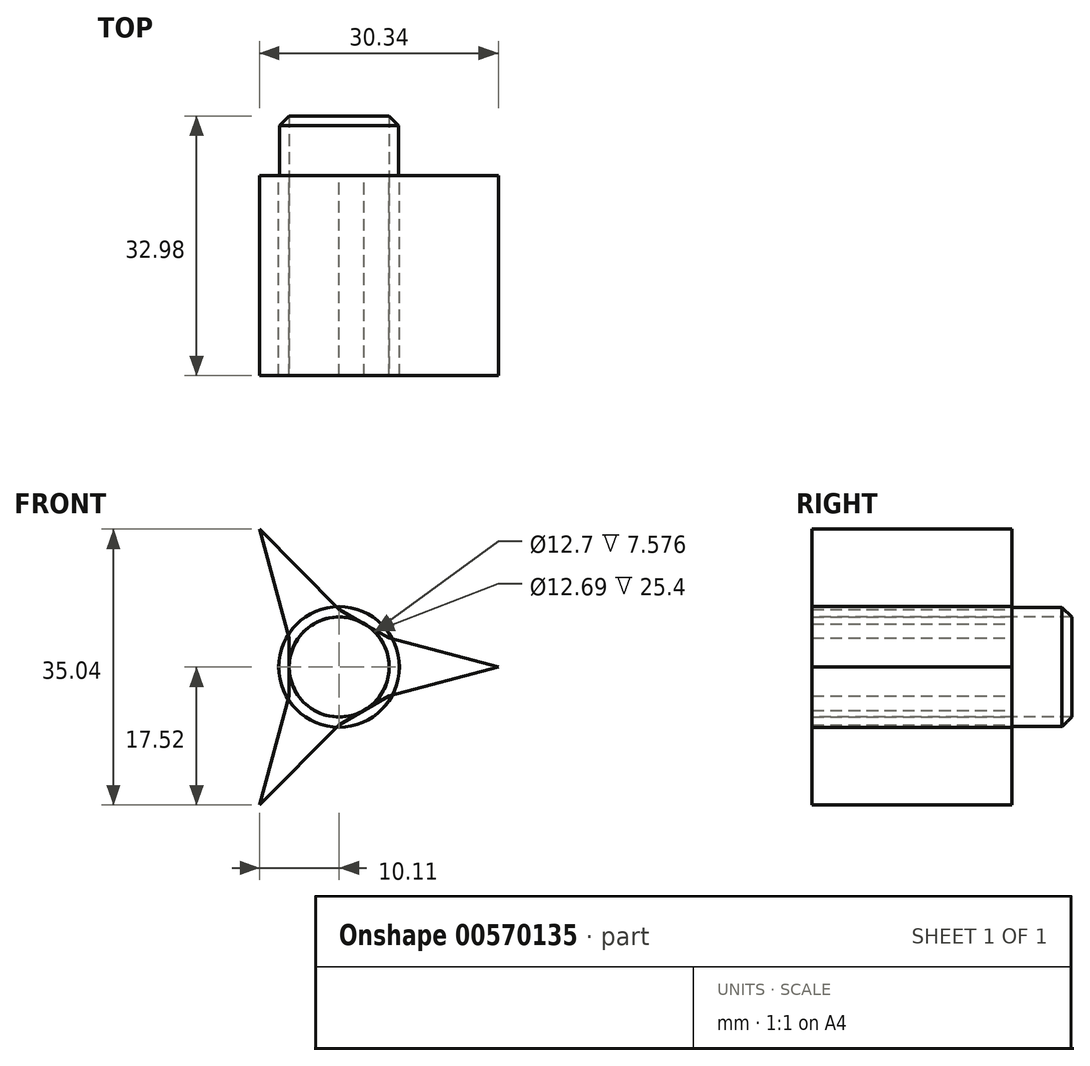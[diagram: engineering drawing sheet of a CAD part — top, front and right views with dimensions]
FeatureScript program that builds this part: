
annotation { "Feature Type Name" : "Feature", "Feature Type Description" : "" }
export const myFeature = defineFeature(function(context is Context, id is Id, definition is map)
    precondition{}
    {
        {
            var Q0;
            Q0=qCreatedBy(makeId("Front.planeOp"),FACE);
            var sketch = newSketch(context, id + "F0", { "sketchPlane" : qUnion([Q0])});
            skCircle(sketch, "E0", {"center": v(0, 0) * mm, "radius": 6.35 * mm});
            skPoint(sketch, "E1.0.midPoint", {"position": v(15.37, 8.44) * mm});
            skArc(sketch, "E2.cCircle", {"start": v(-8.14, 15.53) * mm, "mid": v(-8.77, 15.18) * mm, "end": v(-9.38, 14.81) * mm, "construction": true});
            skCircle(sketch, "E3.cCircle", {"center": v(0, 0) * mm, "radius": 6.35 * mm, "construction": true});
            skLineSegment(sketch, "E3.0", {"start": v(6.35, 3.67) * mm, "end": v(6.35, -3.67) * mm});
            skLineSegment(sketch, "E3.1", {"start": v(6.35, -3.67) * mm, "end": v(0, -7.33) * mm});
            skLineSegment(sketch, "E3.2", {"start": v(0, -7.33) * mm, "end": v(-6.35, -3.67) * mm});
            skLineSegment(sketch, "E3.3", {"start": v(-6.35, -3.67) * mm, "end": v(-6.35, 3.67) * mm});
            skLineSegment(sketch, "E3.4", {"start": v(-6.35, 3.67) * mm, "end": v(0, 7.33) * mm});
            skLineSegment(sketch, "E3.5", {"start": v(0, 7.33) * mm, "end": v(6.35, 3.67) * mm});
            skPoint(sketch, "E3.0.midPoint", {"position": v(6.35, 0) * mm});
            skLineSegment(sketch, "E4", {"start": v(-10.11, 17.52) * mm, "end": v(-6.35, 3.67) * mm});
            skLineSegment(sketch, "E5", {"start": v(-10.11, 17.52) * mm, "end": v(0, 7.33) * mm});
            skLineSegment(sketch, "E6", {"start": v(6.35, 3.67) * mm, "end": v(20.23, 0) * mm});
            skLineSegment(sketch, "E7", {"start": v(6.35, -3.67) * mm, "end": v(20.23, 0) * mm});
            skLineSegment(sketch, "E8", {"start": v(0, -7.33) * mm, "end": v(-10.11, -17.52) * mm});
            skLineSegment(sketch, "E9", {"start": v(-6.35, -3.67) * mm, "end": v(-10.11, -17.52) * mm});
            skPoint(sketch, "E10.orphan", {"position": v(10.5, 16.88) * mm});
            skArc(sketch, "E11.trimOffspring", {"start": v(17.52, -0.72) * mm, "mid": v(17.53, 0) * mm, "end": v(17.52, 0.72) * mm, "construction": true});
            skArc(sketch, "E12.trimOffspring", {"start": v(-9.38, -14.81) * mm, "mid": v(-8.77, -15.18) * mm, "end": v(-8.14, -15.53) * mm, "construction": true});
            skPoint(sketch, "E13.orphan", {"position": v(-20.16, -0.24) * mm});
            skSolve(sketch);
        }
        {
            var Q0;
            {var subQ0=sQuery(id+"F0.wireOp",EDGE,"E4");Q0=makeQuery(id+"F0.imprint","IMPRINT",FACE,{"disambiguationData":[TD([[makeQuery(id+"F0.imprint","IMPRINT",EDGE,{"derivedFrom":subQ0}),1.0]])]});}
            var Q1;
            {var subQ0=sQuery(id+"F0.wireOp",EDGE,"E6");Q1=makeQuery(id+"F0.imprint","IMPRINT",FACE,{"disambiguationData":[TD([[makeQuery(id+"F0.imprint","IMPRINT",EDGE,{"derivedFrom":subQ0}),-1.0]])]});}
            var Q2;
            {var subQ0=sQuery(id+"F0.wireOp",EDGE,"E8");Q2=makeQuery(id+"F0.imprint","IMPRINT",FACE,{"disambiguationData":[TD([[makeQuery(id+"F0.imprint","IMPRINT",EDGE,{"derivedFrom":subQ0}),-1.0]])]});}
            var Q3;
            {var subQ0=sQuery(id+"F0.wireOp",EDGE,"E3.3");var subQ1=sQuery(id+"F0.wireOp",EDGE,"E0");var subQ2=makeQuery(id+"F0.imprint","INTERSECT",VERTEX,{"derivedFrom":[subQ1,subQ0]});Q3=makeQuery(id+"F0.imprint","IMPRINT",FACE,{"disambiguationData":[TD([[makeQuery(id+"F0.imprint","IMPRINT",EDGE,{"disambiguationData":[TD([[subQ2,-1.0]])],"derivedFrom":subQ1}),-1.0]])]});}
            var Q4;
            {var subQ0=sQuery(id+"F0.wireOp",EDGE,"E3.3");var subQ1=sQuery(id+"F0.wireOp",EDGE,"E0");var subQ2=makeQuery(id+"F0.imprint","INTERSECT",VERTEX,{"derivedFrom":[subQ1,subQ0]});Q4=makeQuery(id+"F0.imprint","IMPRINT",FACE,{"disambiguationData":[TD([[makeQuery(id+"F0.imprint","IMPRINT",EDGE,{"disambiguationData":[TD([[subQ2,1.0]])],"derivedFrom":subQ1}),-1.0]])]});}
            var Q5;
            {var subQ0=sQuery(id+"F0.wireOp",EDGE,"E3.5");var subQ1=sQuery(id+"F0.wireOp",EDGE,"E0");var subQ2=makeQuery(id+"F0.imprint","INTERSECT",VERTEX,{"derivedFrom":[subQ1,subQ0]});Q5=makeQuery(id+"F0.imprint","IMPRINT",FACE,{"disambiguationData":[TD([[makeQuery(id+"F0.imprint","IMPRINT",EDGE,{"disambiguationData":[TD([[subQ2,-1.0]])],"derivedFrom":subQ1}),-1.0]])]});}
            var Q6;
            {var subQ0=sQuery(id+"F0.wireOp",EDGE,"E3.5");var subQ1=sQuery(id+"F0.wireOp",EDGE,"E0");var subQ2=makeQuery(id+"F0.imprint","INTERSECT",VERTEX,{"derivedFrom":[subQ1,subQ0]});Q6=makeQuery(id+"F0.imprint","IMPRINT",FACE,{"disambiguationData":[TD([[makeQuery(id+"F0.imprint","IMPRINT",EDGE,{"disambiguationData":[TD([[subQ2,1.0]])],"derivedFrom":subQ1}),-1.0]])]});}
            var Q7;
            {var subQ0=sQuery(id+"F0.wireOp",EDGE,"E3.1");var subQ1=sQuery(id+"F0.wireOp",EDGE,"E0");var subQ2=makeQuery(id+"F0.imprint","INTERSECT",VERTEX,{"derivedFrom":[subQ1,subQ0]});Q7=makeQuery(id+"F0.imprint","IMPRINT",FACE,{"disambiguationData":[TD([[makeQuery(id+"F0.imprint","IMPRINT",EDGE,{"disambiguationData":[TD([[subQ2,-1.0]])],"derivedFrom":subQ1}),-1.0]])]});}
            var Q8;
            {var subQ0=sQuery(id+"F0.wireOp",EDGE,"E3.1");var subQ1=sQuery(id+"F0.wireOp",EDGE,"E0");var subQ2=makeQuery(id+"F0.imprint","INTERSECT",VERTEX,{"derivedFrom":[subQ1,subQ0]});Q8=makeQuery(id+"F0.imprint","IMPRINT",FACE,{"disambiguationData":[TD([[makeQuery(id+"F0.imprint","IMPRINT",EDGE,{"disambiguationData":[TD([[subQ2,1.0]])],"derivedFrom":subQ1}),-1.0]])]});}
            extrude(context, id + "F1", {"entities" : qUnion([Q0, Q1, Q2, Q3, Q4, Q5, Q6, Q7, Q8]), "depth" : 25.4 * mm, "offsetDistance" : 25.4 * mm});
        }
        {
            var Q0;
            Q0=qCreatedBy(makeId("Front.planeOp"),FACE);
            var sketch = newSketch(context, id + "F2", { "sketchPlane" : qUnion([Q0])});
            skCircle(sketch, "E14", {"center": v(0, 0) * mm, "radius": 7.66 * mm});
            skSolve(sketch);
        }
        {
            var Q0;
            Q0=makeQuery(id+"F2.imprint","IMPRINT",FACE,{"disambiguationData":[TD([[makeQuery(id+"F2.imprint","IMPRINT",EDGE,{"derivedFrom":sQuery(id+"F2.wireOp",EDGE,"E14")}),1.0]])]});
            extrude(context, id + "F3", {"entities" : qUnion([Q0]), "depth" : 25.4 * mm, "offsetDistance" : 25.4 * mm});
        }
        {
            var Q0;
            Q0=qCreatedBy(makeId("Front.planeOp"),FACE);
            var sketch = newSketch(context, id + "F4", { "sketchPlane" : qUnion([Q0])});
            skCircle(sketch, "E15", {"center": v(0, 0) * mm, "radius": 6.35 * mm});
            skCircle(sketch, "E16", {"center": v(0, 0) * mm, "radius": 7.58 * mm});
            skSolve(sketch);
        }
        {
            var Q0;
            Q0=makeQuery(id+"F4.imprint","IMPRINT",FACE,{"disambiguationData":[TD([[makeQuery(id+"F4.imprint","IMPRINT",EDGE,{"derivedFrom":sQuery(id+"F4.wireOp",EDGE,"E15")}),-1.0]])]});
            extrude(context, id + "F5", {"entities" : qUnion([Q0]), "oppositeDirection" : true, "depth" : 8.9 * mm, "offsetDistance" : 25.4 * mm});
        }
        {
            var Q0;
            Q0=makeQuery(id+"F5.opExtrude","CAP_EDGE",EDGE,{"disambiguationData":[OSD([sQuery(id+"F4.wireOp",EDGE,"E16")])],"isStart":false});
            chamfer(context, id + "F6", {"entities" : qUnion([Q0]), "width" : 2.54 * mm, "tangentPropagation" : true});
        }
        {
            var Q0;
            Q0=makeQuery(id+"F3.opExtrude","CAP_FACE",FACE,{"disambiguationData":[OSD([sQuery(id+"F2.wireOp",EDGE,"E14")])],"isStart":false});
            var sketch = newSketch(context, id + "F7", { "sketchPlane" : qUnion([Q0])});
            skCircle(sketch, "E17", {"center": v(0, 0) * mm, "radius": 6.34 * mm});
            skSolve(sketch);
        }
        {
            var Q0;
            Q0=makeQuery(id+"F7.imprint","IMPRINT",FACE,{"disambiguationData":[TD([[makeQuery(id+"F7.imprint","IMPRINT",EDGE,{"derivedFrom":sQuery(id+"F7.wireOp",EDGE,"E17")}),1.0]])]});
            extrude(context, id + "F8", {"entities" : qUnion([Q0]), "operationType" : NewBodyOperationType.REMOVE, "endBound" : BoundingType.THROUGH_ALL, "oppositeDirection" : true, "depth" : 25.4 * mm, "offsetDistance" : 25.4 * mm});
        }
    });
